# Revit family: Hager-Univers-IP44-D205-H1250-Cl.II-Encl-NoHosted-PL-en
name_source: partatom
category: Equipement électrique
units: mm (PartAtom-declared; Revit-internal decimal feet)

## family parameters
Basée sur le plan de construction = Oui
Configuration du panneau = Deux colonnes, circuits au sein
Cote de connecteur circulaire = Utiliser le diamètre
Couper avec des vides une fois chargée = Non
Partagée = Non
Point de calcul de pièce = Non
Toujours verticalement = Oui
Type d'élément = Tableau de raccordement

## types (5) — shared parameters
Commentaires du type = Univers
EF000003 - Mounting method = EV000384 - Surface mounted (plaster)
EF000007 - Colour = EV000202 - White
EF000040 - Height = 1250 mm  [stored 4.10105 ft]
EF000049 - Depth = 205 mm  [stored 0.672572 ft]
EF000116 - RAL-number = 9010
EF000118 - With mounting plate = Non
EF000218 - Built-in depth = 205 mm  [stored 0.672572 ft]
EF000266 - Number of rows = 8
EF001088 - Extension possible = Oui
EF001596 - Material housing = EV000179 - Steel
EF001613 - Circuit integrity = EV000494 - None
EF003532 - Suitable for outdoor use = Non
EF004293 - Impact strength = EV006815 - IK09
EF005474 - Degree of protection (IP) = EV006418 - IP44
EF006244 - Transparent cover/door = Non
EF006306 - With lock = Non
EF007800 - Suitable for lightning protection = Non
EF008873 - Nominal current (In) = 250 A
EF009170 - Material plate thickness cabinet = 1 mm  [stored 0.00328084 ft]
EF009171 - Material plate thickness door/cover = 1 mm  [stored 0.00328084 ft]
EF009212 - Cover model = EV000116 - Closed
EF015940 - Cover with overpressure release = Non
Elévation par défaut = 1219 mm  [stored 3.99934 ft]
Fabricant = Hager
HG000002 - With door or cover = Oui
HG000003 - Range = Univers
HG000006 - Flush mounted = Non
HG000023 - Double section enclosure = Non
HG000024 - Bottom section height = 600 mm
HG000026 - Floor standing = Non
zero-valued in all types: HG000027 - Plinth height

## per-type parameters (varying)
| type | EF000008 - Width | EF000339 - Type of cover | EF000437 - Number of conduit inlets | EF001131 - Internal depth | EF002950 - Width in number of modular spacings | EF004427 - Number of modules | EF004464 - Type of door | EF009554 - Number of openings for flange plates | HG000004 - Manufacturer reference | HG000009 - Double swing door | HG000010 - Asymmetric doors |
| Surface mounted (plaster) IP44 W1050 H1250 D205  - FP84SN2 | 1050 mm | EV004216 - Door | 8 | 130 mm  [stored 0.426509 ft] | 48 | 384 | EV003602 - Double | 8 | FP84SN2 | Oui | Non |
| Surface mounted (plaster) IP44 W1300 H1250 D205  - FP85SN2 | 1300 mm  [stored 4.26509 ft] | EV004216 - Door | 10 | 130 mm  [stored 0.426509 ft] | 60 | 480 | EV003602 - Double | 10 | FP85SN2 | Oui | Oui |
| Surface mounted (plaster) IP44 W300 H1250 D205  - FP81SN2 | 300 mm | EV001012 - Cover | 2 | 143 mm | 12 | 96 | EV002646 - Single | 2 | FP81SN2 | Non | Non |
| Surface mounted (plaster) IP44 W550 H1250 D205  - FP82SN2 | 550 mm | EV001012 - Cover | 4 | 143 mm | 24 | 192 | EV002646 - Single | 4 | FP82SN2 | Non | Non |
| Surface mounted (plaster) IP44 W800 H1250 D205  - FP83SN2 | 800 mm  [stored 2.62467 ft] | EV004216 - Door | 6 | 130 mm  [stored 0.426509 ft] | 36 | 288 | EV002646 - Single | 6 | FP83SN2 | Non | Non |

note: [stored X ft] marks values corroborated as IEEE doubles in the binary element streams (Revit-internal decimal feet)

## geometry (parser evidence)
native form markers: Blend x4, Sweep x11
no freeform markers — native parametric forms only
